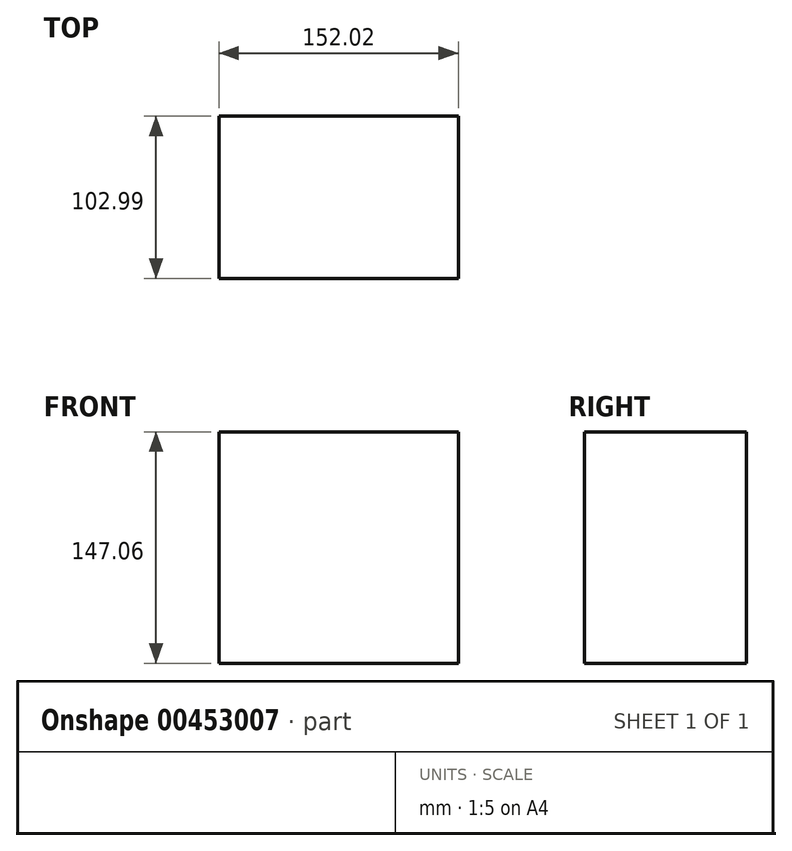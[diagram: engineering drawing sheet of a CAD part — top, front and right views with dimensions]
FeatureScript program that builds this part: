
annotation { "Feature Type Name" : "Feature", "Feature Type Description" : "" }
export const myFeature = defineFeature(function(context is Context, id is Id, definition is map)
    precondition{}
    {
        {
            var Q0;
            Q0=qCreatedBy(makeId("Front.planeOp"),FACE);
            var sketch = newSketch(context, id + "F0", { "sketchPlane" : qUnion([Q0])});
            skLineSegment(sketch, "E0.bottom", {"start": v(-74.93, 0) * mm, "end": v(77.1, 0) * mm});
            skLineSegment(sketch, "E0.top", {"start": v(-74.93, 73.53) * mm, "end": v(77.1, 73.53) * mm});
            skLineSegment(sketch, "E0.left", {"start": v(-74.93, 0) * mm, "end": v(-74.93, 73.53) * mm});
            skLineSegment(sketch, "E0.right", {"start": v(77.1, 0) * mm, "end": v(77.1, 73.53) * mm});
            skLineSegment(sketch, "E1.MirrorCS", {"start": v(-74.93, -73.53) * mm, "end": v(77.1, -73.53) * mm});
            skLineSegment(sketch, "E2.MirrorCS", {"start": v(77.1, 0) * mm, "end": v(77.1, -73.53) * mm});
            skLineSegment(sketch, "E3.MirrorCS", {"start": v(-74.93, 0) * mm, "end": v(-74.93, -73.53) * mm});
            skSolve(sketch);
        }
        {
            var Q0;
            Q0 = qSketchRegion(id + "FFDvaGCDuuMVw4f_0", true);
            var Q1;
            Q1=makeQuery(id+"F0.imprint","IMPRINT",FACE,{"disambiguationData":[TD([[makeQuery(id+"F0.imprint","IMPRINT",EDGE,{"derivedFrom":sQuery(id+"F0.wireOp",EDGE,"E0.bottom")}),-1.0]])]});
            var Q2;
            Q2=makeQuery(id+"F0.imprint","IMPRINT",FACE,{"disambiguationData":[TD([[makeQuery(id+"F0.imprint","IMPRINT",EDGE,{"derivedFrom":sQuery(id+"F0.wireOp",EDGE,"E0.bottom")}),1.0]])]});
            extrude(context, id + "F1", {"entities" : qUnion([Q0, Q1, Q2]), "oppositeDirection" : true, "depth" : 102.99 * mm});
        }
    });
